# Revit family: QF_ZANUSSI_602351_Z1IREDOMES
name_source: partatom
category: Specialty Equipment
units: mm (PartAtom-declared; Revit-internal decimal feet)

## family parameters
Always vertical = Yes
Cut with Voids When Loaded = No
Enable Cutting in Views = No
Maintain Annotation Orientation = No
Part Type = Normal
Room Calculation Point = No
Round Connector Dimension = Use Diameter
Shared = No
Work Plane-Based = No

## types (1)
- Standard
    Accessory = No
    Cold Water Size = 0 mm
    Compressed Air Pressure = 0.0 Pa
    Compressed Air Size = 0 mm
    Compressed Air Volume = 0.0 L/s
    Condensate Return Size = 0 mm
    Cycle = 50 Hz
    Default Elevation = 0 mm  [stored 0 ft]
    Depth Actual = 600 mm
    Description = PLUG-IN INDUCTION GRIDDLE XL, STAINLESS STEEL SMOOTH PLATE - 3-PHASE
    Direct Waste Size = 0 mm
    Gas KW = 0
    Gas Size = 0 mm
    HP = 9.4 HP
    Height Actual = 227 mm  [stored 0.744751 ft]
    Hot Water Size = 0 mm
    Item Number = 602351
    Length Actual = 800 mm  [stored 2.62467 ft]
    Manufacturer = Zanussi
    Model = Z1IREDOMES
    Phase = 3
    Steam Pounds per Hour = 0
    Steam Supply Maximum Pressure = 0.0 Pa
    Steam Supply Minimum Pressure = 0.0 Pa
    Steam Supply Size = 0 mm
    URL = http://www.zanussiprofessional.com
    URL Manufacturer = http://www.zanussiprofessional.com
    Volts = 380 V
    Watts = 0 W
    Weight = 48.00 kg

note: [stored X ft] marks values corroborated as IEEE doubles in the binary element streams (Revit-internal decimal feet)

## geometry (parser evidence)
native form markers: Blend x4
no freeform markers — native parametric forms only
